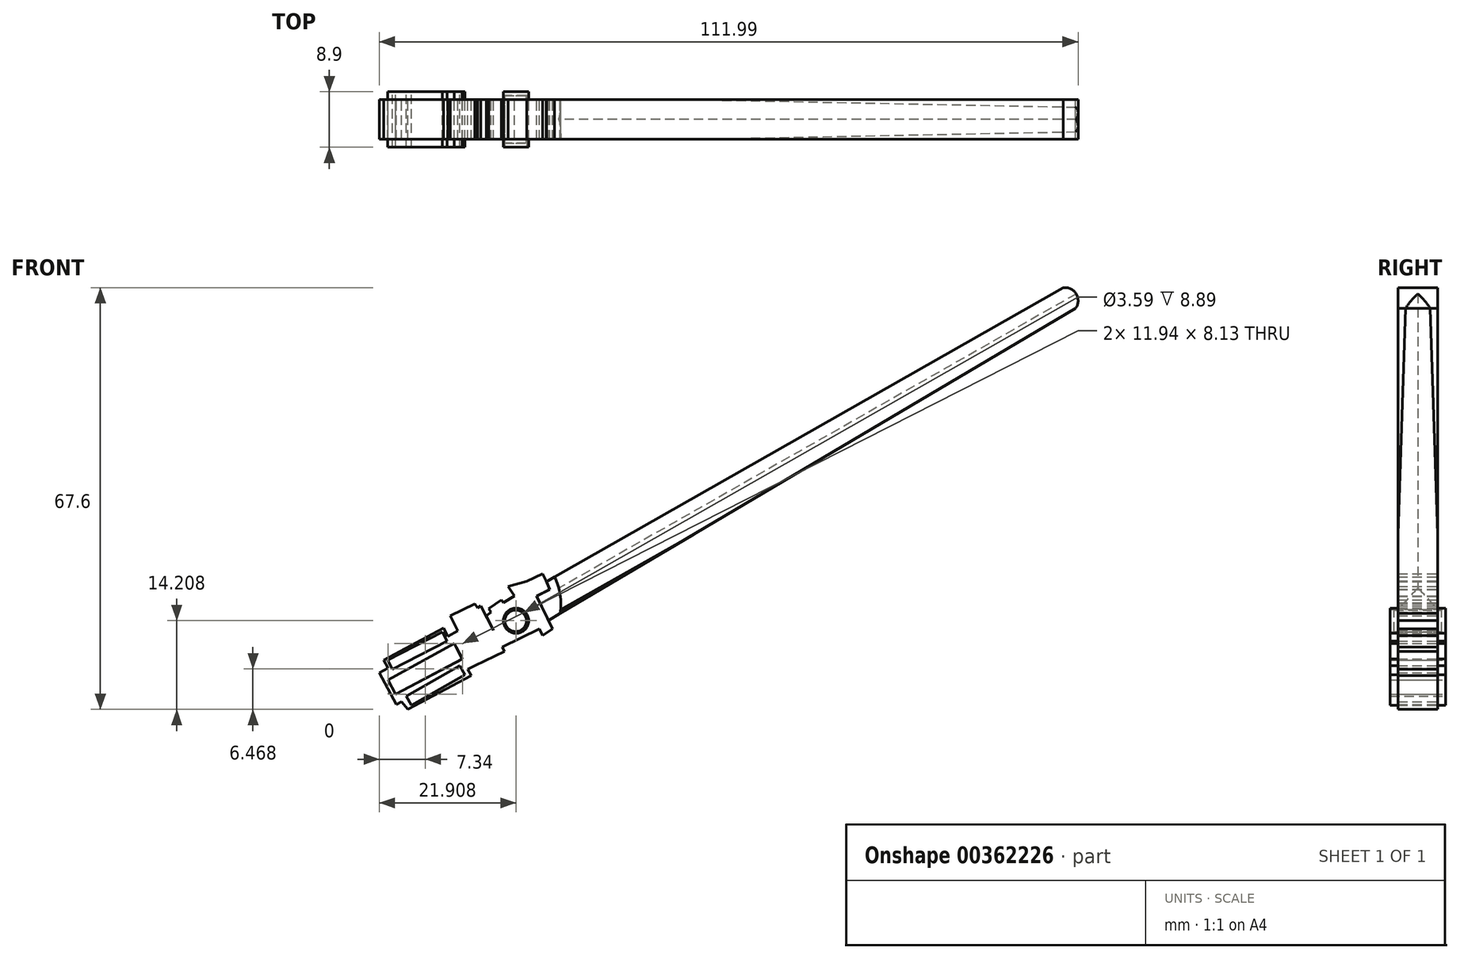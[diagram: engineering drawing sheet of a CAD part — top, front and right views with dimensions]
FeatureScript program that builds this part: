
annotation { "Feature Type Name" : "Feature", "Feature Type Description" : "" }
export const myFeature = defineFeature(function(context is Context, id is Id, definition is map)
    precondition{}
    {
        {
            var Q0;
            Q0=qCreatedBy(makeId("Front.planeOp"),FACE);
            var sketch = newSketch(context, id + "F0", { "sketchPlane" : qUnion([Q0])});
            skLineSegment(sketch, "E0", {"start": v(-26.99, -12.66) * mm, "end": v(54.55, 33.7) * mm});
            skArc(sketch, "E1", {"start": v(56.51, 30.36) * mm, "mid": v(56.65, 32.69) * mm, "end": v(54.55, 33.7) * mm});
            skLineSegment(sketch, "E2", {"start": v(56.51, 30.36) * mm, "end": v(-26.07, -18.47) * mm});
            skArc(sketch, "E3", {"start": v(-26.07, -18.47) * mm, "mid": v(-26.07, -15.5) * mm, "end": v(-26.99, -12.66) * mm});
            skLineSegment(sketch, "E4", {"start": v(-26.99, -12.66) * mm, "end": v(-28.31, -13.3) * mm});
            skLineSegment(sketch, "E5", {"start": v(-28.31, -13.3) * mm, "end": v(-28.88, -12.14) * mm});
            skLineSegment(sketch, "E6", {"start": v(-28.88, -12.14) * mm, "end": v(-31.44, -13.39) * mm});
            skLineSegment(sketch, "E7", {"start": v(-31.44, -13.39) * mm, "end": v(-29.87, -15.7) * mm});
            skLineSegment(sketch, "E8", {"start": v(-29.87, -15.7) * mm, "end": v(-27.76, -14.67) * mm});
            skLineSegment(sketch, "E9", {"start": v(-27.76, -14.67) * mm, "end": v(-28.31, -13.3) * mm});
            skLineSegment(sketch, "E10", {"start": v(-29.87, -15.7) * mm, "end": v(-27.56, -20.44) * mm});
            skLineSegment(sketch, "E11", {"start": v(-27.56, -20.44) * mm, "end": v(-27.29, -21) * mm});
            skLineSegment(sketch, "E12", {"start": v(-27.29, -21) * mm, "end": v(-28.88, -22.08) * mm});
            skLineSegment(sketch, "E13", {"start": v(-28.88, -22.08) * mm, "end": v(-30.44, -18.86) * mm});
            skLineSegment(sketch, "E14", {"start": v(-29.4, -21) * mm, "end": v(-35.45, -23.94) * mm});
            skLineSegment(sketch, "E15", {"start": v(-35.45, -23.94) * mm, "end": v(-37.92, -18.86) * mm});
            skLineSegment(sketch, "E16", {"start": v(-37.92, -18.86) * mm, "end": v(-37.14, -18.34) * mm});
            skLineSegment(sketch, "E17", {"start": v(-37.14, -18.34) * mm, "end": v(-37.55, -17.74) * mm});
            skLineSegment(sketch, "E18", {"start": v(-37.55, -17.74) * mm, "end": v(-35.47, -16.32) * mm});
            skLineSegment(sketch, "E19", {"start": v(-35.47, -16.32) * mm, "end": v(-34.74, -17.39) * mm});
            skLineSegment(sketch, "E20", {"start": v(-34.74, -17.39) * mm, "end": v(-37.14, -18.34) * mm});
            skLineSegment(sketch, "E21", {"start": v(-37.14, -18.34) * mm, "end": v(-36.4, -18.86) * mm});
            skLineSegment(sketch, "E22", {"start": v(-36.4, -18.86) * mm, "end": v(-32.52, -16.98) * mm});
            skLineSegment(sketch, "E23", {"start": v(-32.52, -16.98) * mm, "end": v(-33.4, -15.7) * mm});
            skLineSegment(sketch, "E24", {"start": v(-33.4, -15.7) * mm, "end": v(-35.47, -16.98) * mm});
            skLineSegment(sketch, "E25", {"start": v(-33.4, -15.7) * mm, "end": v(-34.43, -14.17) * mm});
            skLineSegment(sketch, "E26", {"start": v(-34.43, -14.17) * mm, "end": v(-31.44, -13.39) * mm});
            skLineSegment(sketch, "E27", {"start": v(-35.45, -23.94) * mm, "end": v(-35, -24.6) * mm});
            skLineSegment(sketch, "E28", {"start": v(-35, -24.6) * mm, "end": v(-39.75, -26.9) * mm});
            skLineSegment(sketch, "E29", {"start": v(-39.75, -26.9) * mm, "end": v(-43.65, -18.86) * mm});
            skLineSegment(sketch, "E30", {"start": v(-43.65, -18.86) * mm, "end": v(-39.77, -16.98) * mm});
            skLineSegment(sketch, "E31", {"start": v(-39.77, -16.98) * mm, "end": v(-39.32, -17.64) * mm});
            skLineSegment(sketch, "E32", {"start": v(-39.32, -17.64) * mm, "end": v(-38.82, -17.3) * mm});
            skLineSegment(sketch, "E33", {"start": v(-38.82, -17.3) * mm, "end": v(-35, -24.6) * mm});
            skLineSegment(sketch, "E34", {"start": v(-42.46, -21.31) * mm, "end": v(-55.05, -28) * mm});
            skLineSegment(sketch, "E35", {"start": v(-55.05, -28) * mm, "end": v(-52.34, -33.1) * mm});
            skLineSegment(sketch, "E36", {"start": v(-52.34, -33.1) * mm, "end": v(-39.75, -26.9) * mm});
            skLineSegment(sketch, "E37", {"start": v(-41.19, -23.94) * mm, "end": v(-53.68, -30.58) * mm});
            skLineSegment(sketch, "E38", {"start": v(-53.68, -29.18) * mm, "end": v(-52.46, -31.48) * mm});
            skLineSegment(sketch, "E39", {"start": v(-52.46, -31.48) * mm, "end": v(-41.74, -25.78) * mm});
            skLineSegment(sketch, "E40", {"start": v(-41.74, -25.78) * mm, "end": v(-43.03, -23.34) * mm});
            skLineSegment(sketch, "E41", {"start": v(-43.03, -23.34) * mm, "end": v(-53.68, -29.18) * mm});
            skLineSegment(sketch, "E42", {"start": v(-53.68, -27.28) * mm, "end": v(-54.38, -25.97) * mm});
            skLineSegment(sketch, "E43", {"start": v(-54.38, -25.97) * mm, "end": v(-44.75, -20.85) * mm});
            skLineSegment(sketch, "E44", {"start": v(-44.75, -20.85) * mm, "end": v(-44.05, -22.16) * mm});
            skLineSegment(sketch, "E45", {"start": v(-40.9, -27.47) * mm, "end": v(-40.63, -28) * mm});
            skLineSegment(sketch, "E46", {"start": v(-40.9, -27.47) * mm, "end": v(-40.35, -28.5) * mm});
            skLineSegment(sketch, "E47", {"start": v(-40.35, -28.5) * mm, "end": v(-50.46, -33.88) * mm});
            skLineSegment(sketch, "E48", {"start": v(-50.46, -33.88) * mm, "end": v(-52.46, -31.48) * mm});
            skLineSegment(sketch, "E49", {"start": v(-55.05, -28) * mm, "end": v(-55.44, -27.28) * mm});
            skLineSegment(sketch, "E50", {"start": v(-55.44, -27.28) * mm, "end": v(-56.32, -28) * mm});
            skLineSegment(sketch, "E51", {"start": v(-56.32, -28) * mm, "end": v(-53.34, -34.13) * mm});
            skLineSegment(sketch, "E52", {"start": v(-53.34, -34.13) * mm, "end": v(-52.34, -33.44) * mm});
            skSolve(sketch);
        }
        {
            var Q0;
            Q0 = qSketchRegion(id + "F0", true);
            extrude(context, id + "F1", {"entities" : qUnion([Q0]), "endBound" : BoundingType.SYMMETRIC, "depth" : 6.35 * mm});
        }
        {
            var Q0;
            Q0 = qSketchRegion(id + "F0", true);
            extrude(context, id + "F2", {"entities" : qUnion([Q0]), "endBound" : BoundingType.SYMMETRIC, "depth" : 6.35 * mm});
        }
        {
            var Q0;
            Q0=qCreatedBy(makeId("Front.planeOp"),FACE);
            var sketch = newSketch(context, id + "F3", { "sketchPlane" : qUnion([Q0])});
            skArc(sketch, "E53", {"start": v(-26.07, -18.5) * mm, "mid": v(-26.07, -15.51) * mm, "end": v(-26.98, -12.67) * mm});
            skLineSegment(sketch, "E54", {"start": v(-26.98, -12.67) * mm, "end": v(-28.23, -13.41) * mm});
            skLineSegment(sketch, "E55", {"start": v(-28.23, -13.41) * mm, "end": v(-27.75, -14.66) * mm});
            skLineSegment(sketch, "E56", {"start": v(-27.75, -14.66) * mm, "end": v(-29.87, -15.75) * mm});
            skLineSegment(sketch, "E57", {"start": v(-26.07, -18.5) * mm, "end": v(-27.93, -19.68) * mm});
            skLineSegment(sketch, "E58", {"start": v(-27.93, -19.68) * mm, "end": v(-29.87, -15.75) * mm});
            skSolve(sketch);
        }
        {
            var Q0;
            Q0 = qSketchRegion(id + "F3", true);
            extrude(context, id + "F4", {"entities" : qUnion([Q0]), "endBound" : BoundingType.SYMMETRIC, "depth" : 6.35 * mm});
        }
        {
            var Q0;
            Q0=qCreatedBy(makeId("Front.planeOp"),FACE);
            var sketch = newSketch(context, id + "F5", { "sketchPlane" : qUnion([Q0])});
            skCircle(sketch, "E59", {"center": v(-33.14, -19.67) * mm, "radius": 2.02 * mm});
            skCircle(sketch, "E60", {"center": v(-33.14, -19.67) * mm, "radius": 1.8 * mm});
            skSolve(sketch);
        }
        {
            var Q0;
            Q0 = qSketchRegion(id + "F5", true);
            extrude(context, id + "F6", {"entities" : qUnion([Q0]), "endBound" : BoundingType.SYMMETRIC, "depth" : 8.9 * mm});
        }
        {
            var Q0;
            Q0=qCreatedBy(makeId("Front.planeOp"),FACE);
            var sketch = newSketch(context, id + "F7", { "sketchPlane" : qUnion([Q0])});
            skLineSegment(sketch, "E61", {"start": v(-43.04, -23.32) * mm, "end": v(-41.76, -25.78) * mm});
            skLineSegment(sketch, "E62", {"start": v(-41.76, -25.78) * mm, "end": v(-52.45, -31.47) * mm});
            skLineSegment(sketch, "E63", {"start": v(-52.45, -31.47) * mm, "end": v(-53.66, -29.2) * mm});
            skLineSegment(sketch, "E64", {"start": v(-53.66, -29.2) * mm, "end": v(-43.04, -23.32) * mm});
            skSolve(sketch);
        }
        {
            var Q0;
            Q0 = qSketchRegion(id + "F7", true);
            extrude(context, id + "F8", {"entities" : qUnion([Q0]), "endBound" : BoundingType.SYMMETRIC, "depth" : 8.9 * mm});
        }
        {
            var Q0;
            Q0=qCreatedBy(makeId("Front.planeOp"),FACE);
            var sketch = newSketch(context, id + "F9", { "sketchPlane" : qUnion([Q0])});
            skLineSegment(sketch, "E65.bottom", {"start": v(-44.18, -22.93) * mm, "end": v(-52.93, -27.48) * mm});
            skLineSegment(sketch, "E65.top", {"start": v(-44.95, -21.46) * mm, "end": v(-53.7, -26.01) * mm});
            skLineSegment(sketch, "E65.left", {"start": v(-44.18, -22.93) * mm, "end": v(-44.95, -21.46) * mm});
            skLineSegment(sketch, "E65.right", {"start": v(-52.93, -27.48) * mm, "end": v(-53.7, -26.01) * mm});
            skPoint(sketch, "E65.middle", {"position": v(-51.68, -21.36) * mm});
            skLineSegment(sketch, "E66", {"start": v(-42.18, -24.04) * mm, "end": v(-42.69, -24.24) * mm});
            skLineSegment(sketch, "E67", {"start": v(-42.69, -24.24) * mm, "end": v(-52.98, -29.6) * mm});
            skLineSegment(sketch, "E68.MirrorCS", {"start": v(-42.15, -26.88) * mm, "end": v(-50.71, -31.77) * mm});
            skLineSegment(sketch, "E69.MirrorCS", {"start": v(-41.33, -28.32) * mm, "end": v(-49.9, -33.21) * mm});
            skLineSegment(sketch, "E70.MirrorCS", {"start": v(-42.15, -26.88) * mm, "end": v(-41.33, -28.32) * mm});
            skLineSegment(sketch, "E71.MirrorCS", {"start": v(-50.71, -31.77) * mm, "end": v(-49.9, -33.21) * mm});
            skSolve(sketch);
        }
        {
            var Q0;
            Q0 = qSketchRegion(id + "F9", true);
            extrude(context, id + "F10", {"entities" : qUnion([Q0]), "endBound" : BoundingType.SYMMETRIC, "depth" : 8.9 * mm});
        }
        {
            var Q0;
            Q0=qCreatedBy(makeId("Front.planeOp"),FACE);
            var sketch = newSketch(context, id + "F11", { "sketchPlane" : qUnion([Q0])});
            skCircle(sketch, "E72", {"center": v(-33.2, -19.7) * mm, "radius": 1.72 * mm});
            skSolve(sketch);
        }
        {
            var Q0;
            Q0 = qSketchRegion(id + "F11", true);
            extrude(context, id + "F12", {"entities" : qUnion([Q0]), "endBound" : BoundingType.SYMMETRIC, "depth" : 7.62 * mm});
        }
        {
            var Q0;
            Q0=makeQuery(id+"F1.opExtrude","CAP_EDGE",EDGE,{"disambiguationData":[OSD([sQuery(id+"F0.wireOp",EDGE,"E0")])],"isStart":true});
            var Q1;
            Q1=makeQuery(id+"F1.opExtrude","CAP_EDGE",EDGE,{"disambiguationData":[OSD([sQuery(id+"F0.wireOp",EDGE,"E0")])],"isStart":false});
            chamfer(context, id + "F13", {"entities" : qUnion([Q0, Q1]), "width" : 5.08 * mm, "tangentPropagation" : true});
        }
    });
